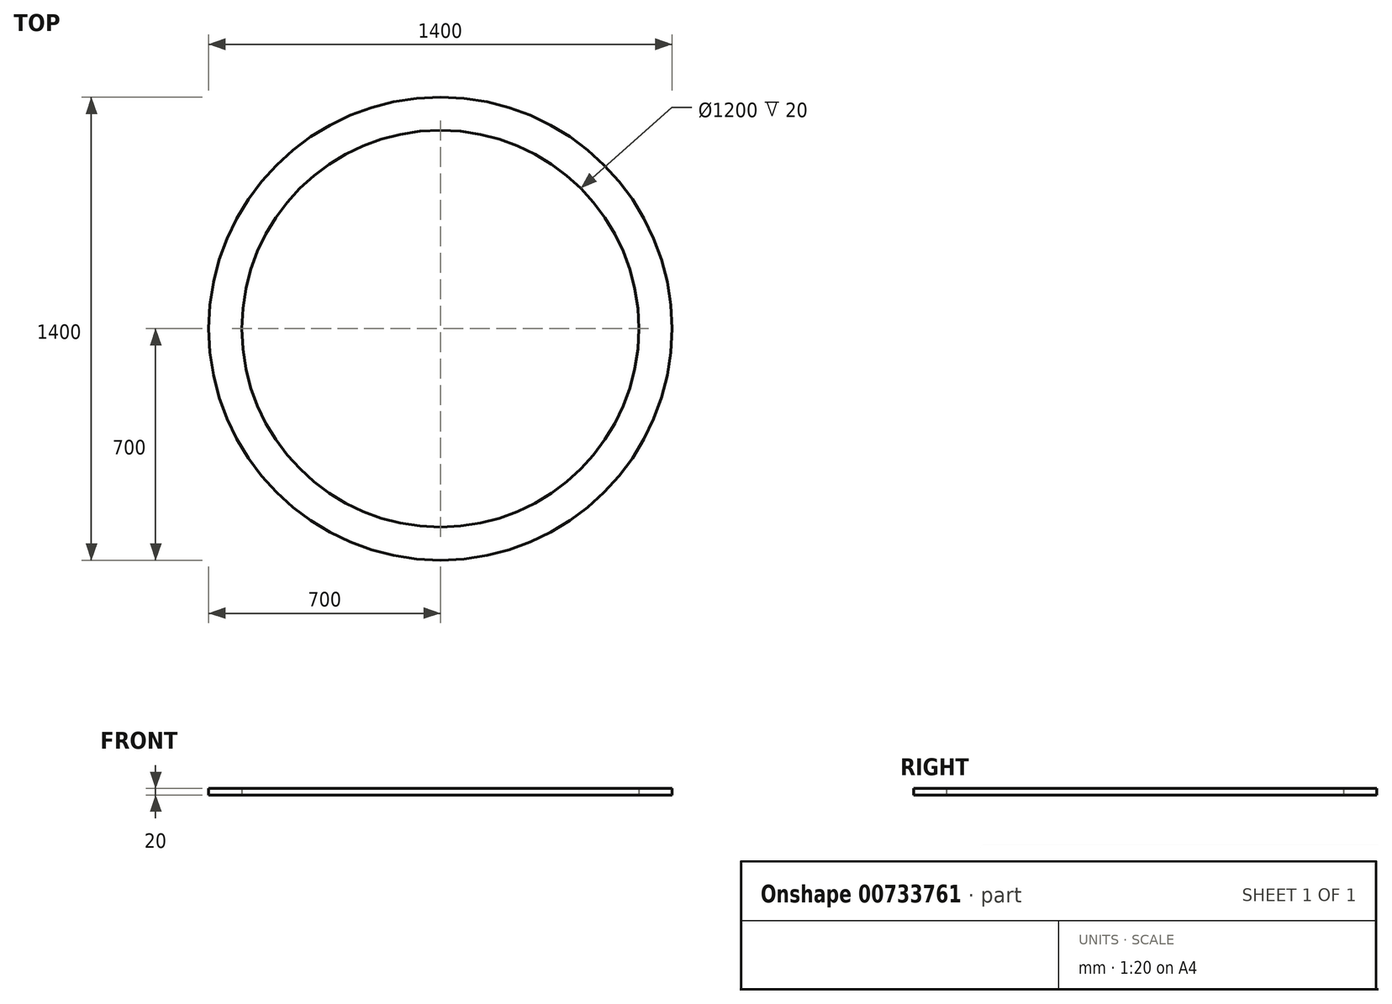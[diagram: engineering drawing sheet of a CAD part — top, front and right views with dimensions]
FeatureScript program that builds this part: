
annotation { "Feature Type Name" : "Feature", "Feature Type Description" : "" }
export const myFeature = defineFeature(function(context is Context, id is Id, definition is map)
    precondition{}
    {
        {
            var Q0;
            Q0=qCreatedBy(makeId("Top.planeOp"),FACE);
            var sketch = newSketch(context, id + "F0", { "sketchPlane" : qUnion([Q0])});
            skArc(sketch, "E0", {"start": v(-600, 0) * mm, "mid": v(-424.26, -424.26) * mm, "end": v(0, -600) * mm});
            skArc(sketch, "E1", {"start": v(-700, 0) * mm, "mid": v(-494.97, -494.97) * mm, "end": v(0, -700) * mm});
            skLineSegment(sketch, "E2", {"start": v(0, 0) * mm, "end": v(0, -700) * mm});
            skLineSegment(sketch, "E3", {"start": v(-600, 0) * mm, "end": v(-700, 0) * mm});
            skLineSegment(sketch, "E4", {"start": v(-600, 0) * mm, "end": v(0, 0) * mm});
            skLineSegment(sketch, "E5.MirrorCS", {"start": v(600, 0) * mm, "end": v(700, 0) * mm});
            skArc(sketch, "E6.MirrorCS", {"start": v(600, 0) * mm, "mid": v(424.26, -424.26) * mm, "end": v(0, -600) * mm});
            skArc(sketch, "E7.MirrorCS", {"start": v(700, 0) * mm, "mid": v(494.97, -494.97) * mm, "end": v(0, -700) * mm});
            skLineSegment(sketch, "E8.MirrorCS", {"start": v(600, 0) * mm, "end": v(0, 0) * mm});
            skLineSegment(sketch, "E9.MirrorCS", {"start": v(0, 0) * mm, "end": v(0, 700) * mm});
            skArc(sketch, "E10.MirrorCS", {"start": v(-600, 0) * mm, "mid": v(-424.26, 424.26) * mm, "end": v(0, 600) * mm});
            skArc(sketch, "E11.MirrorCS", {"start": v(600, 0) * mm, "mid": v(424.26, 424.26) * mm, "end": v(0, 600) * mm});
            skArc(sketch, "E12.MirrorCS", {"start": v(700, 0) * mm, "mid": v(494.97, 494.97) * mm, "end": v(0, 700) * mm});
            skArc(sketch, "E13.MirrorCS", {"start": v(-700, 0) * mm, "mid": v(-494.97, 494.97) * mm, "end": v(0, 700) * mm});
            skSolve(sketch);
        }
        {
            var Q0;
            Q0=qSketchRegion(id+"F0",true);
            extrude(context, id + "F1", {"entities" : qUnion([Q0]), "depth" : 20 * mm, "offsetDistance" : 25 * mm});
        }
    });
